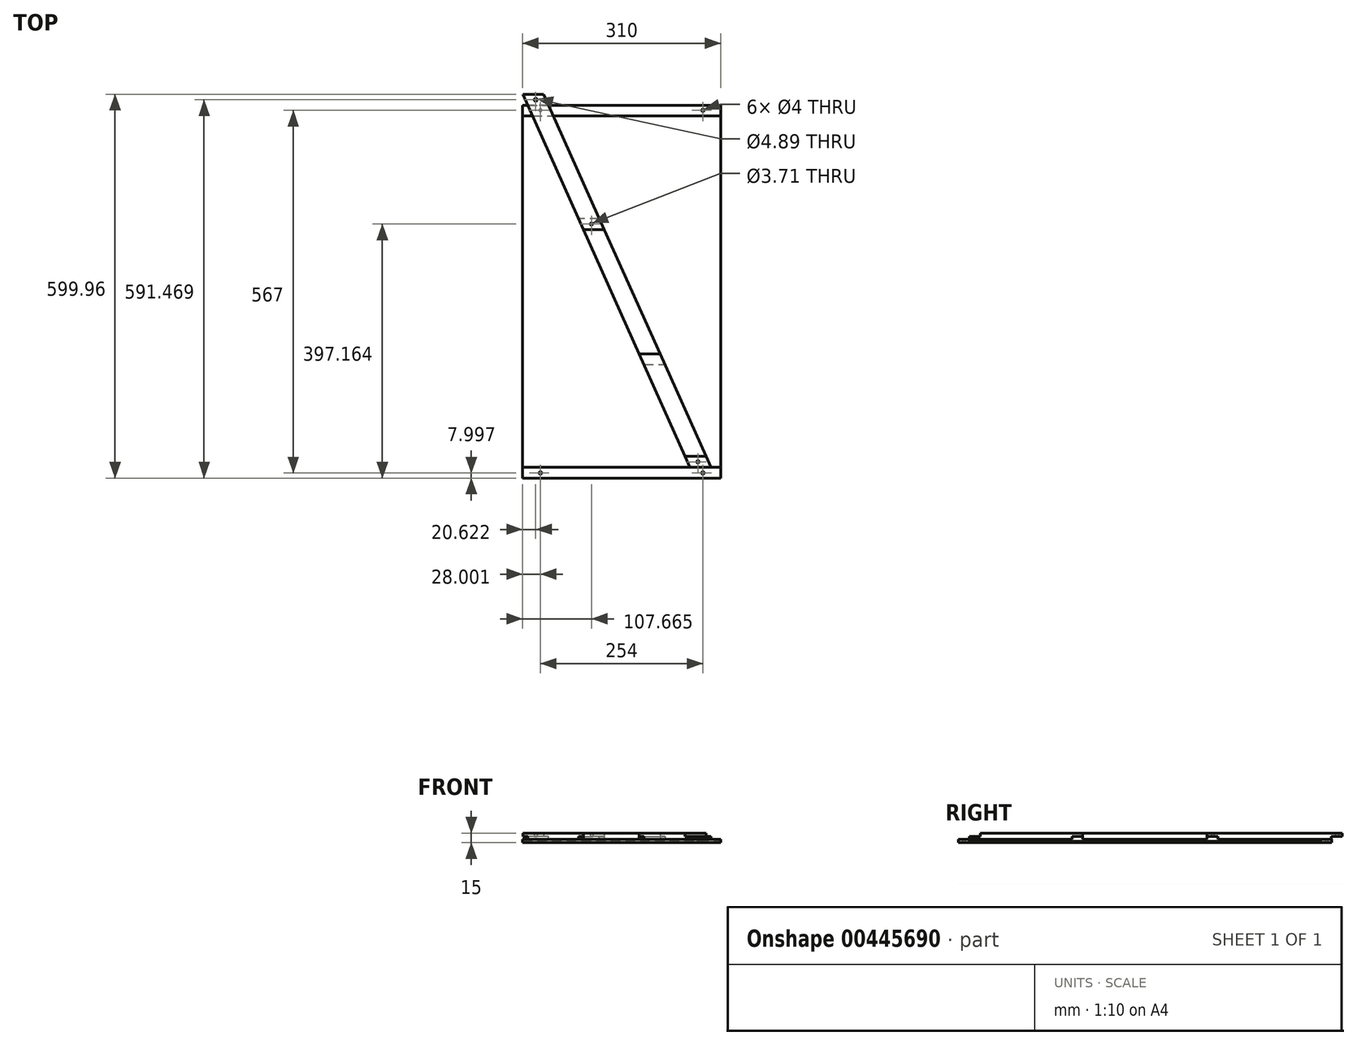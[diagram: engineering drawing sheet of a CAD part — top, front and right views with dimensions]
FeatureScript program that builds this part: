
annotation { "Feature Type Name" : "Feature", "Feature Type Description" : "" }
export const myFeature = defineFeature(function(context is Context, id is Id, definition is map)
    precondition{}
    {
        {
            var Q0;
            Q0=qCreatedBy(makeId("Top.planeOp"),FACE);
            var sketch = newSketch(context, id + "F0", { "sketchPlane" : qUnion([Q0])});
            skLineSegment(sketch, "E0.bottom", {"start": v(-146.94, 292.25) * mm, "end": v(163.06, 292.25) * mm});
            skLineSegment(sketch, "E0.top", {"start": v(-146.94, -290.75) * mm, "end": v(163.06, -290.75) * mm});
            skLineSegment(sketch, "E0.left", {"start": v(-146.94, 292.25) * mm, "end": v(-146.94, -290.75) * mm});
            skLineSegment(sketch, "E0.right", {"start": v(163.06, 292.25) * mm, "end": v(163.06, -290.75) * mm});
            skLineSegment(sketch, "E1.bottom", {"start": v(-146.94, -273.75) * mm, "end": v(163.06, -273.75) * mm});
            skLineSegment(sketch, "E1.left", {"start": v(-146.94, -273.75) * mm, "end": v(-146.94, -290.75) * mm});
            skLineSegment(sketch, "E1.right", {"start": v(163.06, -273.75) * mm, "end": v(163.06, -290.75) * mm});
            skLineSegment(sketch, "E2.top", {"start": v(-146.94, 275.25) * mm, "end": v(163.06, 275.25) * mm});
            skLineSegment(sketch, "E2.left", {"start": v(-146.94, 292.25) * mm, "end": v(-146.94, 275.25) * mm});
            skLineSegment(sketch, "E2.right", {"start": v(163.06, 292.25) * mm, "end": v(163.06, 275.25) * mm});
            skCircle(sketch, "E3", {"center": v(-118.94, 284.25) * mm, "radius": 2 * mm});
            skCircle(sketch, "E4", {"center": v(-118.94, -282.75) * mm, "radius": 2 * mm});
            skCircle(sketch, "E5", {"center": v(135.06, -282.75) * mm, "radius": 2 * mm});
            skCircle(sketch, "E6", {"center": v(135.06, 284.25) * mm, "radius": 2 * mm});
            skSolve(sketch);
        }
        {
            var Q0;
            Q0=makeQuery(id+"F0.imprint","IMPRINT",FACE,{"disambiguationData":[TD([[makeQuery(id+"F0.imprint","IMPRINT",EDGE,{"derivedFrom":sQuery(id+"F0.wireOp",EDGE,"E0.bottom")}),-1.0]])]});
            var Q1;
            Q1=makeQuery(id+"F0.imprint","IMPRINT",FACE,{"disambiguationData":[TD([[makeQuery(id+"F0.imprint","IMPRINT",EDGE,{"derivedFrom":sQuery(id+"F0.wireOp",EDGE,"E1.bottom")}),-1.0]])]});
            extrude(context, id + "F1", {"entities" : qUnion([Q0, Q1]), "depth" : 5 * mm});
        }
        {
            var Q0;
            Q0=makeQuery(id+"F0.imprint","IMPRINT",FACE,{"disambiguationData":[TD([[makeQuery(id+"F0.imprint","IMPRINT",EDGE,{"derivedFrom":sQuery(id+"F0.wireOp",EDGE,"E0.left")}),1.0]])]});
            extrude(context, id + "F2", {"entities" : qUnion([Q0]), "operationType" : NewBodyOperationType.ADD, "depth" : 2 * mm});
        }
        {
            var Q0;
            Q0=makeQuery(id+"F1.opExtrude","CAP_FACE",FACE,{"disambiguationData":[OSD([sQuery(id+"F0.wireOp",EDGE,"E0.bottom"),sQuery(id+"F0.wireOp",EDGE,"E2.top"),sQuery(id+"F0.wireOp",EDGE,"E2.left"),sQuery(id+"F0.wireOp",EDGE,"E2.right"),sQuery(id+"F0.wireOp",EDGE,"E3"),sQuery(id+"F0.wireOp",EDGE,"E6")])],"isStart":false});
            var sketch = newSketch(context, id + "F3", { "sketchPlane" : qUnion([Q0])});
            skLineSegment(sketch, "E7", {"start": v(-146.56, 309.21) * mm, "end": v(114.6, -273.79) * mm});
            skLineSegment(sketch, "E8", {"start": v(147.48, -273.79) * mm, "end": v(-106.09, 292.25) * mm});
            skLineSegment(sketch, "E9", {"start": v(-106.09, 292.25) * mm, "end": v(-106.09, 292.25) * mm});
            skLineSegment(sketch, "E10", {"start": v(114.6, -273.79) * mm, "end": v(147.48, -273.79) * mm});
            skLineSegment(sketch, "E11", {"start": v(114.58, -273.73) * mm, "end": v(147.46, -273.73) * mm});
            skLineSegment(sketch, "E12", {"start": v(35.15, -96.42) * mm, "end": v(68.02, -96.42) * mm});
            skLineSegment(sketch, "E13", {"start": v(-51.9, 97.91) * mm, "end": v(-19.03, 97.91) * mm});
            skLineSegment(sketch, "E14", {"start": v(-113.69, 309.21) * mm, "end": v(403.67, 309.21) * mm, "construction": true});
            skLineSegment(sketch, "E15", {"start": v(-113.69, 309.21) * mm, "end": v(-146.56, 309.21) * mm});
            skLineSegment(sketch, "E16", {"start": v(-106.09, 292.25) * mm, "end": v(-113.69, 309.21) * mm});
            skSolve(sketch);
        }
        {
            var Q0;
            {var subQ0=sQuery(id+"F3.wireOp",EDGE,"E10");Q0=makeQuery(id+"F3.imprint","IMPRINT",FACE,{"disambiguationData":[TD([[makeQuery(id+"F3.imprint","IMPRINT",EDGE,{"derivedFrom":subQ0}),1.0]])]});}
            var Q1;
            {var subQ0=sQuery(id+"F3.wireOp",EDGE,"E11");Q1=makeQuery(id+"F3.imprint","IMPRINT",FACE,{"disambiguationData":[TD([[makeQuery(id+"F3.imprint","IMPRINT",EDGE,{"derivedFrom":subQ0}),1.0]])]});}
            var Q2;
            {var subQ0=sQuery(id+"F3.wireOp",EDGE,"E13");Q2=makeQuery(id+"F3.imprint","IMPRINT",FACE,{"disambiguationData":[TD([[makeQuery(id+"F3.imprint","IMPRINT",EDGE,{"derivedFrom":subQ0}),1.0]])]});}
            var Q3;
            {var subQ0=sQuery(id+"F3.wireOp",EDGE,"J1muQc5M-LaKd-R3UE-bVF6-yMRndZ3wfCzE");Q3=makeQuery(id+"F3.imprint","IMPRINT",FACE,{"disambiguationData":[TD([[makeQuery(id+"F3.imprint","IMPRINT",EDGE,{"derivedFrom":subQ0}),1.0]])]});}
            var Q4;
            {var subQ4=sQuery(id+"F3.wireOp",EDGE,"6IFBYwRl-OV4b-qpfd-9Sut-i4lfYgeIs6Dc");Q4=makeQuery(id+"F3.imprint","IMPRINT",FACE,{"disambiguationData":[TD([[makeQuery(id+"F3.imprint","IMPRINT",EDGE,{"derivedFrom":subQ4}),1.0]])]});}
            var Q5;
            Q5=makeQuery(id+"F3.imprint","IMPRINT",FACE,{"disambiguationData":[TD([[makeQuery(id+"F3.imprint","IMPRINT",EDGE,{"derivedFrom":makeQuery(id+"F1.opExtrude","CAP_EDGE",EDGE,{"disambiguationData":[OSD([sQuery(id+"F0.wireOp",EDGE,"E3")])],"isStart":false})}),-1.0]])]});
            var Q6;
            {var subQ0=sQuery(id+"F3.wireOp",EDGE,"E15");Q6=makeQuery(id+"F3.imprint","IMPRINT",FACE,{"disambiguationData":[TD([[makeQuery(id+"F3.imprint","IMPRINT",EDGE,{"derivedFrom":subQ0}),1.0]])]});}
            var Q7;
            Q7=makeQuery(id+"F3.imprint","IMPRINT",FACE,{"disambiguationData":[TD([[makeQuery(id+"F3.imprint","IMPRINT",EDGE,{"derivedFrom":makeQuery(id+"F1.opExtrude","CAP_EDGE",EDGE,{"disambiguationData":[OSD([sQuery(id+"F0.wireOp",EDGE,"E3")])],"isStart":false})}),1.0]])]});
            extrude(context, id + "F4", {"entities" : qUnion([Q0, Q1, Q2, Q3, Q4, Q5, Q6, Q7]), "depth" : 10 * mm});
        }
        {
            var Q0;
            Q0=makeQuery(id+"F4.opExtrude","CAP_FACE",FACE,{"disambiguationData":[OSD([sQuery(id+"F3.wireOp",EDGE,"E7"),sQuery(id+"F3.wireOp",EDGE,"E8"),sQuery(id+"F3.wireOp",EDGE,"E10"),sQuery(id+"F3.wireOp",EDGE,"E12")])],"isStart":false});
            var sketch = newSketch(context, id + "F5", { "sketchPlane" : qUnion([Q0])});
            skLineSegment(sketch, "E17.bottom", {"start": v(147.48, -273.79) * mm, "end": v(103.31, -273.79) * mm});
            skLineSegment(sketch, "E17.top", {"start": v(147.48, -256.79) * mm, "end": v(103.31, -256.79) * mm});
            skLineSegment(sketch, "E17.left", {"start": v(147.48, -273.79) * mm, "end": v(147.48, -256.79) * mm});
            skLineSegment(sketch, "E17.right", {"start": v(103.31, -273.79) * mm, "end": v(103.31, -256.79) * mm});
            skSolve(sketch);
        }
        {
            var Q0;
            {var subQ1=makeQuery(id+"F4.opExtrude","CAP_EDGE",EDGE,{"disambiguationData":[OSD([sQuery(id+"F3.wireOp",EDGE,"E8")])],"isStart":false});var subQ5=sQuery(id+"F5.wireOp",EDGE,"E17.top");var subQ6=makeQuery(id+"F5.imprint","INTERSECT",VERTEX,{"derivedFrom":[subQ1,subQ5]});Q0=makeQuery(id+"F5.imprint","IMPRINT",FACE,{"disambiguationData":[TD([[makeQuery(id+"F5.imprint","IMPRINT",EDGE,{"disambiguationData":[TD([[subQ6,-1.0]])],"derivedFrom":subQ5}),1.0]])]});}
            extrude(context, id + "F6", {"entities" : qUnion([Q0]), "operationType" : NewBodyOperationType.REMOVE, "oppositeDirection" : true, "depth" : 5 * mm});
        }
        {
            var Q0;
            {var subQ0=sQuery(id+"F3.wireOp",EDGE,"E11");Q0=makeQuery(id+"F3.imprint","IMPRINT",FACE,{"disambiguationData":[TD([[makeQuery(id+"F3.imprint","IMPRINT",EDGE,{"derivedFrom":subQ0}),1.0]])]});}
            var sketch = newSketch(context, id + "F7", { "sketchPlane" : qUnion([Q0])});
            skLineSegment(sketch, "E18.bottom", {"start": v(27.66, -96.42) * mm, "end": v(87.28, -96.42) * mm});
            skLineSegment(sketch, "E18.top", {"start": v(27.66, -113.42) * mm, "end": v(87.28, -113.42) * mm});
            skLineSegment(sketch, "E18.left", {"start": v(27.66, -96.42) * mm, "end": v(27.66, -113.42) * mm});
            skLineSegment(sketch, "E18.right", {"start": v(87.28, -96.42) * mm, "end": v(87.28, -113.42) * mm});
            skSolve(sketch);
        }
        {
            var Q0;
            {var subQ0=sQuery(id+"F7.wireOp",EDGE,"E18.bottom");var subQ1=sQuery(id+"F3.wireOp",EDGE,"E11");var subQ2=sQuery(id+"F3.wireOp",EDGE,"E7");var subQ4=makeQuery(id+"F3.imprint","IMPRINT",EDGE,{"disambiguationData":[TD([[makeQuery(id+"F3.imprint","INTERSECT",VERTEX,{"derivedFrom":[subQ2,subQ1]}),1.0]])],"derivedFrom":subQ2});var subQ5=makeQuery(id+"F7.imprint","INTERSECT",VERTEX,{"derivedFrom":[subQ4,subQ0]});Q0=makeQuery(id+"F7.imprint","IMPRINT",FACE,{"disambiguationData":[TD([[makeQuery(id+"F7.imprint","IMPRINT",EDGE,{"disambiguationData":[TD([[subQ5,-1.0]])],"derivedFrom":subQ0}),-1.0]])]});}
            extrude(context, id + "F8", {"entities" : qUnion([Q0]), "operationType" : NewBodyOperationType.REMOVE, "depth" : 5 * mm});
        }
        {
            var Q0;
            Q0=makeQuery(id+"F6.boolean.opBoolean","COPY",FACE,{"derivedFrom":makeQuery(id+"F6.opExtrude","CAP_FACE",FACE,{"disambiguationData":[OSD([sQuery(id+"F3.wireOp",EDGE,"E7"),sQuery(id+"F3.wireOp",EDGE,"E8"),sQuery(id+"F5.wireOp",EDGE,"E17.bottom"),sQuery(id+"F5.wireOp",EDGE,"E17.top")])],"isStart":false})});
            var sketch = newSketch(context, id + "F9", { "sketchPlane" : qUnion([Q0])});
            skCircle(sketch, "E19", {"center": v(127.24, -265.29) * mm, "radius": 2 * mm});
            skSolve(sketch);
        }
        {
            var Q0;
            Q0=makeQuery(id+"F9.imprint","IMPRINT",FACE,{"disambiguationData":[TD([[makeQuery(id+"F9.imprint","IMPRINT",EDGE,{"derivedFrom":sQuery(id+"F9.wireOp",EDGE,"E19")}),1.0]])]});
            extrude(context, id + "F10", {"entities" : qUnion([Q0]), "operationType" : NewBodyOperationType.REMOVE, "oppositeDirection" : true, "depth" : 25 * mm});
        }
        {
            var Q0;
            Q0=makeQuery(id+"F4.opExtrude","CAP_FACE",FACE,{"disambiguationData":[OSD([sQuery(id+"F3.wireOp",EDGE,"E7"),sQuery(id+"F3.wireOp",EDGE,"E8"),sQuery(id+"F3.wireOp",EDGE,"E13"),sQuery(id+"F3.wireOp",EDGE,"E15"),sQuery(id+"F3.wireOp",EDGE,"E16")])],"isStart":false});
            var sketch = newSketch(context, id + "F11", { "sketchPlane" : qUnion([Q0])});
            skLineSegment(sketch, "E20.bottom", {"start": v(-71.93, 309.21) * mm, "end": v(-168.39, 309.21) * mm});
            skLineSegment(sketch, "E20.left", {"start": v(-71.93, 309.21) * mm, "end": v(-71.93, 292.21) * mm});
            skLineSegment(sketch, "E21.bottom", {"start": v(6.64, 114.91) * mm, "end": v(-72.85, 114.91) * mm});
            skLineSegment(sketch, "E21.top", {"start": v(6.64, 97.91) * mm, "end": v(-72.85, 97.91) * mm});
            skLineSegment(sketch, "E21.left", {"start": v(6.64, 114.91) * mm, "end": v(6.64, 97.91) * mm});
            skLineSegment(sketch, "E21.right", {"start": v(-72.85, 114.91) * mm, "end": v(-72.85, 97.91) * mm});
            skLineSegment(sketch, "E22.bottom", {"start": v(-95.75, 309.22) * mm, "end": v(-168.39, 309.22) * mm});
            skLineSegment(sketch, "E22.top", {"start": v(-95.75, 292.22) * mm, "end": v(-168.39, 292.22) * mm});
            skLineSegment(sketch, "E22.left", {"start": v(-95.75, 309.22) * mm, "end": v(-95.75, 292.22) * mm});
            skLineSegment(sketch, "E22.right", {"start": v(-168.39, 309.22) * mm, "end": v(-168.39, 292.22) * mm});
            skSolve(sketch);
        }
        {
            var Q0;
            {var subQ1=makeQuery(id+"F4.opExtrude","CAP_EDGE",EDGE,{"disambiguationData":[OSD([sQuery(id+"F3.wireOp",EDGE,"E8"),sQuery(id+"F3.wireOp",EDGE,"E16")])],"isStart":false});var subQ8=sQuery(id+"F11.wireOp",EDGE,"E21.top");var subQ10=makeQuery(id+"F11.imprint","INTERSECT",VERTEX,{"derivedFrom":[subQ1,subQ8]});Q0=makeQuery(id+"F11.imprint","IMPRINT",FACE,{"disambiguationData":[TD([[makeQuery(id+"F11.imprint","IMPRINT",EDGE,{"disambiguationData":[TD([[subQ10,-1.0]])],"derivedFrom":subQ1}),1.0]])]});}
            var Q1;
            {var subQ0=sQuery(id+"F11.wireOp",EDGE,"E20.bottom");var subQ6=makeQuery(id+"F4.opExtrude","CAP_EDGE",EDGE,{"disambiguationData":[OSD([sQuery(id+"F3.wireOp",EDGE,"E8"),sQuery(id+"F3.wireOp",EDGE,"E16")])],"isStart":false});var subQ7=makeQuery(id+"F11.imprint","INTERSECT",VERTEX,{"derivedFrom":[subQ6,subQ0]});Q1=makeQuery(id+"F11.imprint","IMPRINT",FACE,{"disambiguationData":[TD([[makeQuery(id+"F11.imprint","IMPRINT",EDGE,{"disambiguationData":[TD([[subQ7,1.0]])],"derivedFrom":subQ6}),1.0]])]});}
            extrude(context, id + "F12", {"entities" : qUnion([Q0, Q1]), "operationType" : NewBodyOperationType.REMOVE, "oppositeDirection" : true, "depth" : 10 * mm, "hasSecondDirection" : true, "secondDirectionOppositeDirection" : true, "secondDirectionDepth" : 5 * mm});
        }
        {
            var Q0;
            {var subQ0=sQuery(id+"F3.wireOp",EDGE,"PvjHYzsI-3cCP-5eiw-7aNb-k65Mr3khq46D");Q0=makeQuery(id+"F3.imprint","IMPRINT",FACE,{"disambiguationData":[TD([[makeQuery(id+"F3.imprint","IMPRINT",EDGE,{"derivedFrom":subQ0}),-1.0]])]});}
            var Q1;
            {var subQ1=sQuery(id+"F3.wireOp",EDGE,"PvjHYzsI-3cCP-5eiw-7aNb-k65Mr3khq46D");Q1=makeQuery(id+"F3.imprint","IMPRINT",FACE,{"disambiguationData":[TD([[makeQuery(id+"F3.imprint","IMPRINT",EDGE,{"derivedFrom":subQ1}),1.0]])]});}
            var Q2;
            {var subQ4=sQuery(id+"F3.wireOp",EDGE,"6IFBYwRl-OV4b-qpfd-9Sut-i4lfYgeIs6Dc");Q2=makeQuery(id+"F3.imprint","IMPRINT",FACE,{"disambiguationData":[TD([[makeQuery(id+"F3.imprint","IMPRINT",EDGE,{"derivedFrom":subQ4}),1.0]])]});}
            var Q3;
            {var subQ0=sQuery(id+"F3.wireOp",EDGE,"E12");Q3=makeQuery(id+"F3.imprint","IMPRINT",FACE,{"disambiguationData":[TD([[makeQuery(id+"F3.imprint","IMPRINT",EDGE,{"derivedFrom":subQ0}),1.0]])]});}
            extrude(context, id + "F13", {"entities" : qUnion([Q0, Q1, Q2, Q3]), "depth" : 10 * mm});
        }
        {
            var Q0;
            {var subQ0=sQuery(id+"F11.wireOp",EDGE,"E21.bottom");var subQ2=sQuery(id+"F3.wireOp",EDGE,"E8");var subQ4=sQuery(id+"F3.wireOp",EDGE,"E13");var subQ5=makeQuery(id+"F3.imprint","IMPRINT",EDGE,{"disambiguationData":[TD([[makeQuery(id+"F3.imprint","INTERSECT",VERTEX,{"derivedFrom":[subQ2,subQ4]}),-1.0]])],"derivedFrom":subQ2});var subQ6=makeQuery(id+"F11.imprint","INTERSECT",VERTEX,{"derivedFrom":[subQ5,subQ0]});Q0=makeQuery(id+"F11.imprint","IMPRINT",FACE,{"disambiguationData":[TD([[makeQuery(id+"F11.imprint","IMPRINT",EDGE,{"disambiguationData":[TD([[subQ6,-1.0]])],"derivedFrom":subQ0}),1.0]])]});}
            var Q1;
            Q1=makeQuery(id+"F11.imprint","IMPRINT",FACE,{"disambiguationData":[TD([[makeQuery(id+"F11.imprint","IMPRINT",EDGE,{"derivedFrom":sQuery(id+"F11.wireOp",EDGE,"E20.bottom")}),1.0]])]});
            extrude(context, id + "F14", {"entities" : qUnion([Q0, Q1]), "operationType" : NewBodyOperationType.REMOVE, "depth" : 5 * mm});
        }
        {
            var Q0;
            Q0=makeQuery(id+"F12.boolean.opBoolean","COPY",FACE,{"derivedFrom":makeQuery(id+"F12.opExtrude","CAP_FACE",FACE,{"disambiguationData":[OSD([sQuery(id+"F3.wireOp",EDGE,"E7"),sQuery(id+"F3.wireOp",EDGE,"E8"),sQuery(id+"F3.wireOp",EDGE,"E16"),sQuery(id+"F11.wireOp",EDGE,"E20.bottom"),sQuery(id+"F11.wireOp",EDGE,"E22.top")])],"isStart":true})});
            var sketch = newSketch(context, id + "F15", { "sketchPlane" : qUnion([Q0])});
            skCircle(sketch, "E23", {"center": v(-126.32, -300.72) * mm, "radius": 2.44 * mm});
            skSolve(sketch);
        }
        {
            var Q0;
            Q0=makeQuery(id+"F15.imprint","IMPRINT",FACE,{"disambiguationData":[TD([[makeQuery(id+"F15.imprint","IMPRINT",EDGE,{"derivedFrom":sQuery(id+"F15.wireOp",EDGE,"E23")}),1.0]])]});
            extrude(context, id + "F16", {"entities" : qUnion([Q0]), "operationType" : NewBodyOperationType.REMOVE, "oppositeDirection" : true, "depth" : 25 * mm});
        }
        {
            var Q0;
            Q0=makeQuery(id+"F12.boolean.opBoolean","COPY",FACE,{"derivedFrom":makeQuery(id+"F12.opExtrude","CAP_FACE",FACE,{"disambiguationData":[OSD([sQuery(id+"F3.wireOp",EDGE,"E7"),sQuery(id+"F3.wireOp",EDGE,"E8"),sQuery(id+"F3.wireOp",EDGE,"E16"),sQuery(id+"F11.wireOp",EDGE,"E21.bottom"),sQuery(id+"F11.wireOp",EDGE,"E21.top")])],"isStart":true})});
            var sketch = newSketch(context, id + "F17", { "sketchPlane" : qUnion([Q0])});
            skCircle(sketch, "E24", {"center": v(-39.27, -106.41) * mm, "radius": 1.86 * mm});
            skSolve(sketch);
        }
        {
            var Q0;
            Q0=makeQuery(id+"F17.imprint","IMPRINT",FACE,{"disambiguationData":[TD([[makeQuery(id+"F17.imprint","IMPRINT",EDGE,{"derivedFrom":sQuery(id+"F17.wireOp",EDGE,"E24")}),1.0]])]});
            extrude(context, id + "F18", {"entities" : qUnion([Q0]), "operationType" : NewBodyOperationType.REMOVE, "oppositeDirection" : true, "depth" : 25 * mm});
        }
    });
